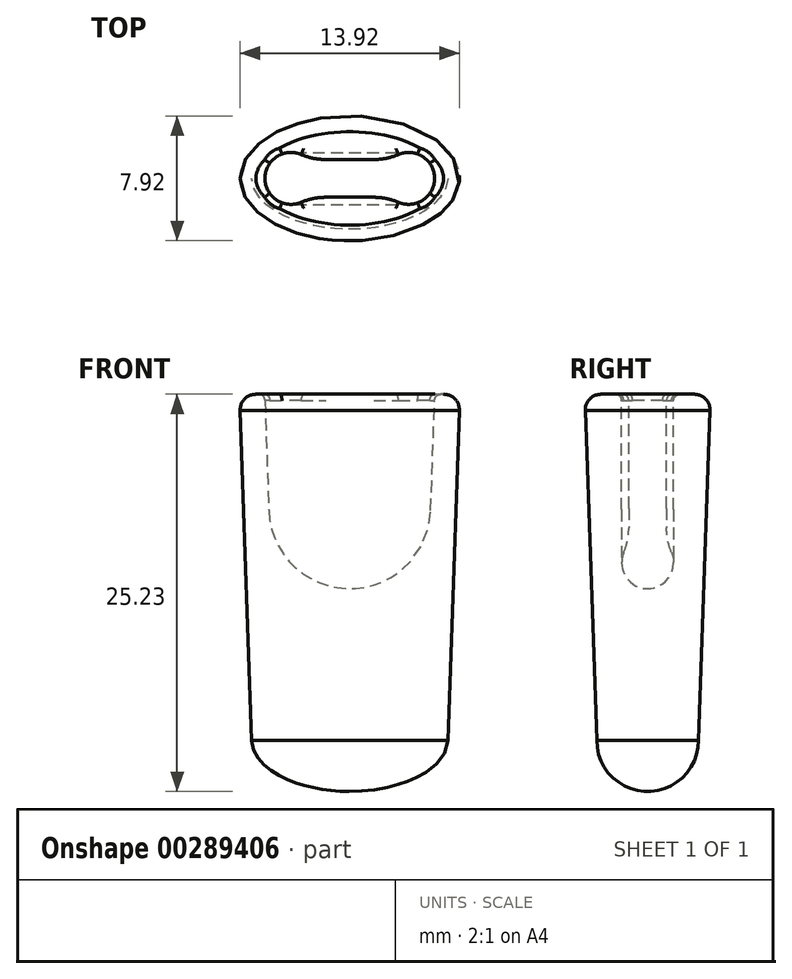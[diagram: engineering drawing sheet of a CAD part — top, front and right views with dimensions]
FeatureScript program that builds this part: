
annotation { "Feature Type Name" : "Feature", "Feature Type Description" : "" }
export const myFeature = defineFeature(function(context is Context, id is Id, definition is map)
    precondition{}
    {
        {
            var Q0;
            Q0=qCreatedBy(makeId("Front.planeOp"),FACE);
            var sketch = newSketch(context, id + "F0", { "sketchPlane" : qUnion([Q0])});
            skLineSegment(sketch, "E0", {"start": v(-3.78, 0.84) * mm, "end": v(-3.5, -7.33) * mm});
            skArc(sketch, "E1", {"start": v(-3.5, -7.33) * mm, "mid": v(-2.43, -9.72) * mm, "end": v(0, -10.7) * mm});
            skLineSegment(sketch, "E2", {"start": v(-3.78, 0.84) * mm, "end": v(-3.78, 1.56) * mm});
            skLineSegment(sketch, "E3", {"start": v(-3.75, 0) * mm, "end": v(0, 0) * mm, "construction": true});
            skLineSegment(sketch, "E4", {"start": v(-3.78, 1.56) * mm, "end": v(0, 1.56) * mm});
            skLineSegment(sketch, "E5.MirrorCS", {"start": v(3.78, 1.56) * mm, "end": v(0, 1.56) * mm});
            skLineSegment(sketch, "E6.MirrorCS", {"start": v(3.78, 0.84) * mm, "end": v(3.78, 1.56) * mm});
            skLineSegment(sketch, "E7.MirrorCS", {"start": v(3.75, 0) * mm, "end": v(0, 0) * mm, "construction": true});
            skLineSegment(sketch, "E8.MirrorCS", {"start": v(3.78, 0.84) * mm, "end": v(3.5, -7.33) * mm});
            skArc(sketch, "E9.MirrorCS", {"start": v(3.5, -7.33) * mm, "mid": v(2.43, -9.72) * mm, "end": v(0, -10.7) * mm});
            skSolve(sketch);
        }
        {
            var Q0;
            Q0=qCreatedBy(makeId("Top.planeOp"),FACE);
            var Q1;
            Q1=sQuery(id+"F0.wireOp",VERTEX,"E5.MirrorCS.end");
            cPlane(context, id + "F1", {"entities" : qUnion([Q0, Q1]), "cplaneType" : CPlaneType.PLANE_POINT, "offset" : 25 * mm, "width" : 150 * mm, "height" : 150 * mm});
        }
        {
            var Q0;
            Q0=qCreatedBy(id+"F1.planeOp",FACE);
            var sketch = newSketch(context, id + "F2", { "sketchPlane" : qUnion([Q0])});
            skCircle(sketch, "E10", {"center": v(-3.78, 0) * mm, "radius": 1.65 * mm});
            skSolve(sketch);
        }
        {
            var Q0;
            Q0=makeQuery(id+"F2.imprint","IMPRINT",FACE,{"disambiguationData":[TD([[makeQuery(id+"F2.imprint","IMPRINT",EDGE,{"derivedFrom":sQuery(id+"F2.wireOp",EDGE,"E10")}),1.0]])]});
            var Q1;
            Q1=sQuery(id+"F0.wireOp",EDGE,"E2");
            var Q2;
            Q2=sQuery(id+"F0.wireOp",EDGE,"E0");
            var Q3;
            Q3=sQuery(id+"F0.wireOp",EDGE,"E1");
            var Q4;
            Q4=sQuery(id+"F0.wireOp",EDGE,"E9.MirrorCS");
            var Q5;
            Q5=sQuery(id+"F0.wireOp",EDGE,"E8.MirrorCS");
            var Q6;
            Q6=sQuery(id+"F0.wireOp",EDGE,"E6.MirrorCS");
            sweep(context, id + "F3", {"profiles" : qUnion([Q0]), "path" : qUnion([Q1, Q2, Q3, Q4, Q5, Q6])});
        }
        {
            var Q0;
            Q0=makeQuery(id+"F0.imprint","IMPRINT",FACE,{"disambiguationData":[TD([[makeQuery(id+"F0.imprint","IMPRINT",EDGE,{"derivedFrom":sQuery(id+"F0.wireOp",EDGE,"E0")}),1.0]])]});
            extrude(context, id + "F4", {"entities" : qUnion([Q0]), "operationType" : NewBodyOperationType.ADD, "endBound" : BoundingType.SYMMETRIC, "depth" : 2.4 * mm});
        }
        {
            var Q0;
            {var subQ0=sQuery(id+"F0.wireOp",EDGE,"b3059032-d9f8-48f3-bb5a-612e4b6044fb0.MirrorCS");Q0=makeQuery(id+"F4.boolean.opBoolean","INTERSECT",EDGE,{"derivedFrom":[makeQuery(id+"F3.opSweep","SWEPT_FACE",FACE,{"disambiguationData":[OSD([subQ0,sQuery(id+"F2.wireOp",EDGE,"E10")])]}),makeQuery(id+"F4.opExtrude","CAP_FACE",FACE,{"disambiguationData":[OSD([sQuery(id+"F0.wireOp",EDGE,"E0"),sQuery(id+"F0.wireOp",EDGE,"E1"),subQ0,sQuery(id+"F0.wireOp",EDGE,"39ebad5e-6162-4d79-9b9c-69094e73386a0.MirrorCS"),sQuery(id+"F0.wireOp",EDGE,"sgdeaiES-GsHM-U3g8-oXAS-PtHumTGgpg0I")])],"isStart":true})]});}
            var Q1;
            {var subQ0=sQuery(id+"F0.wireOp",EDGE,"E0");Q1=makeQuery(id+"F4.boolean.opBoolean","INTERSECT",EDGE,{"derivedFrom":[makeQuery(id+"F3.opSweep","SWEPT_FACE",FACE,{"disambiguationData":[OSD([subQ0,sQuery(id+"F2.wireOp",EDGE,"E10")])]}),makeQuery(id+"F4.opExtrude","CAP_FACE",FACE,{"disambiguationData":[OSD([subQ0,sQuery(id+"F0.wireOp",EDGE,"E1"),sQuery(id+"F0.wireOp",EDGE,"b3059032-d9f8-48f3-bb5a-612e4b6044fb0.MirrorCS"),sQuery(id+"F0.wireOp",EDGE,"39ebad5e-6162-4d79-9b9c-69094e73386a0.MirrorCS"),sQuery(id+"F0.wireOp",EDGE,"sgdeaiES-GsHM-U3g8-oXAS-PtHumTGgpg0I")])],"isStart":true})]});}
            var Q2;
            {var subQ0=sQuery(id+"F0.wireOp",EDGE,"E1");Q2=makeQuery(id+"F4.boolean.opBoolean","INTERSECT",EDGE,{"derivedFrom":[makeQuery(id+"F3.opSweep","SWEPT_FACE",FACE,{"disambiguationData":[OSD([subQ0,sQuery(id+"F2.wireOp",EDGE,"E10")])]}),makeQuery(id+"F4.opExtrude","CAP_FACE",FACE,{"disambiguationData":[OSD([sQuery(id+"F0.wireOp",EDGE,"E0"),subQ0,sQuery(id+"F0.wireOp",EDGE,"b3059032-d9f8-48f3-bb5a-612e4b6044fb0.MirrorCS"),sQuery(id+"F0.wireOp",EDGE,"39ebad5e-6162-4d79-9b9c-69094e73386a0.MirrorCS"),sQuery(id+"F0.wireOp",EDGE,"sgdeaiES-GsHM-U3g8-oXAS-PtHumTGgpg0I")])],"isStart":true})]});}
            var Q3;
            {var subQ0=sQuery(id+"F0.wireOp",EDGE,"b3059032-d9f8-48f3-bb5a-612e4b6044fb0.MirrorCS");Q3=makeQuery(id+"F4.boolean.opBoolean","INTERSECT",EDGE,{"derivedFrom":[makeQuery(id+"F3.opSweep","SWEPT_FACE",FACE,{"disambiguationData":[OSD([subQ0,sQuery(id+"F2.wireOp",EDGE,"E10")])]}),makeQuery(id+"F4.opExtrude","CAP_FACE",FACE,{"disambiguationData":[OSD([sQuery(id+"F0.wireOp",EDGE,"E0"),sQuery(id+"F0.wireOp",EDGE,"E1"),subQ0,sQuery(id+"F0.wireOp",EDGE,"39ebad5e-6162-4d79-9b9c-69094e73386a0.MirrorCS"),sQuery(id+"F0.wireOp",EDGE,"sgdeaiES-GsHM-U3g8-oXAS-PtHumTGgpg0I")])],"isStart":false})]});}
            var Q4;
            {var subQ0=sQuery(id+"F0.wireOp",EDGE,"E0");Q4=makeQuery(id+"F4.boolean.opBoolean","INTERSECT",EDGE,{"derivedFrom":[makeQuery(id+"F3.opSweep","SWEPT_FACE",FACE,{"disambiguationData":[OSD([subQ0,sQuery(id+"F2.wireOp",EDGE,"E10")])]}),makeQuery(id+"F4.opExtrude","CAP_FACE",FACE,{"disambiguationData":[OSD([subQ0,sQuery(id+"F0.wireOp",EDGE,"E1"),sQuery(id+"F0.wireOp",EDGE,"b3059032-d9f8-48f3-bb5a-612e4b6044fb0.MirrorCS"),sQuery(id+"F0.wireOp",EDGE,"39ebad5e-6162-4d79-9b9c-69094e73386a0.MirrorCS"),sQuery(id+"F0.wireOp",EDGE,"sgdeaiES-GsHM-U3g8-oXAS-PtHumTGgpg0I")])],"isStart":false})]});}
            var Q5;
            {var subQ0=sQuery(id+"F0.wireOp",EDGE,"E1");Q5=makeQuery(id+"F4.boolean.opBoolean","INTERSECT",EDGE,{"derivedFrom":[makeQuery(id+"F3.opSweep","SWEPT_FACE",FACE,{"disambiguationData":[OSD([subQ0,sQuery(id+"F2.wireOp",EDGE,"E10")])]}),makeQuery(id+"F4.opExtrude","CAP_FACE",FACE,{"disambiguationData":[OSD([sQuery(id+"F0.wireOp",EDGE,"E0"),subQ0,sQuery(id+"F0.wireOp",EDGE,"b3059032-d9f8-48f3-bb5a-612e4b6044fb0.MirrorCS"),sQuery(id+"F0.wireOp",EDGE,"39ebad5e-6162-4d79-9b9c-69094e73386a0.MirrorCS"),sQuery(id+"F0.wireOp",EDGE,"sgdeaiES-GsHM-U3g8-oXAS-PtHumTGgpg0I")])],"isStart":false})]});}
            fillet(context, id + "F5", {"entities" : qUnion([Q0, Q1, Q2, Q3, Q4, Q5]), "radius" : 4 * mm, "tangentPropagation" : true, "allowEdgeOverflow" : false});
        }
        {
            var Q0;
            Q0=qCreatedBy(makeId("Top.planeOp"),FACE);
            var sketch = newSketch(context, id + "F6", { "sketchPlane" : qUnion([Q0])});
            skEllipse(sketch, "E11", {"center": v(0, 0) * mm, "majorRadius": 7 * mm, "minorRadius": 4 * mm, "majorAxis": v(1, 0)});
            skPoint(sketch, "E12", {"position": v(-7, 0) * mm});
            skSolve(sketch);
        }
        {
            var Q0;
            Q0=makeQuery(id+"F6.imprint","IMPRINT",FACE,{"disambiguationData":[TD([[makeQuery(id+"F6.imprint","IMPRINT",EDGE,{"derivedFrom":sQuery(id+"F6.wireOp",EDGE,"E11")}),1.0]])]});
            extrude(context, id + "F7", {"entities" : qUnion([Q0]), "oppositeDirection" : true, "depth" : 22 * mm, "hasDraft" : true, "draftAngle" : 2 * degree, "draftPullDirection" : true});
        }
        {
            var Q0;
            Q0=makeQuery(id+"F7.opExtrude","CAP_FACE",FACE,{"disambiguationData":[OSD([sQuery(id+"F6.wireOp",EDGE,"E11")])],"isStart":false});
            var sketch = newSketch(context, id + "F8", { "sketchPlane" : qUnion([Q0])});
            skLineSegment(sketch, "E13", {"start": v(-6.23, 0) * mm, "end": v(6.23, 0) * mm});
            skFitSpline(sketch, "E14", {"points": [v(-27.2, 0) * mm, v(-27.2, 0.3) * mm, v(-27.18, 0.62) * mm, v(-27.05, 1.24) * mm, v(-26.96, 1.56) * mm, v(-26.7, 2.22) * mm, v(-26.53, 2.56) * mm, v(-26.11, 3.25) * mm, v(-25.86, 3.6) * mm, v(-24.98, 4.67) * mm, v(-24.2, 5.4) * mm, v(-22.33, 6.8) * mm, v(-21.22, 7.48) * mm, v(-18.7, 8.74) * mm, v(-17.3, 9.31) * mm, v(-14.26, 10.33) * mm, v(-12.63, 10.77) * mm, v(-9.2, 11.48) * mm, v(-7.4, 11.75) * mm, v(-3.74, 12.11) * mm, v(-1.87, 12.2) * mm, v(1.87, 12.2) * mm, v(3.74, 12.11) * mm, v(7.4, 11.75) * mm, v(9.2, 11.48) * mm, v(12.63, 10.77) * mm, v(14.26, 10.33) * mm, v(17.3, 9.31) * mm, v(18.7, 8.74) * mm, v(21.22, 7.48) * mm, v(22.33, 6.8) * mm, v(24.2, 5.4) * mm, v(24.98, 4.67) * mm, v(25.86, 3.6) * mm, v(26.11, 3.25) * mm, v(26.53, 2.56) * mm, v(26.7, 2.22) * mm, v(26.96, 1.56) * mm, v(27.05, 1.24) * mm, v(27.18, 0.62) * mm, v(27.2, 0.3) * mm, v(27.2, 0) * mm, v(27.2, -0.3) * mm, v(27.18, -0.62) * mm, v(27.05, -1.24) * mm, v(26.96, -1.56) * mm, v(26.7, -2.22) * mm, v(26.53, -2.56) * mm, v(26.11, -3.25) * mm, v(25.86, -3.6) * mm, v(24.98, -4.67) * mm, v(24.2, -5.4) * mm, v(22.33, -6.8) * mm, v(21.22, -7.48) * mm, v(18.7, -8.74) * mm, v(17.3, -9.31) * mm, v(14.26, -10.33) * mm, v(12.63, -10.77) * mm, v(9.2, -11.48) * mm, v(7.4, -11.75) * mm, v(3.74, -12.11) * mm, v(1.87, -12.2) * mm, v(-1.87, -12.2) * mm, v(-3.74, -12.11) * mm, v(-7.4, -11.75) * mm, v(-9.2, -11.48) * mm, v(-12.63, -10.77) * mm, v(-14.26, -10.33) * mm, v(-17.3, -9.31) * mm, v(-18.7, -8.74) * mm, v(-21.22, -7.48) * mm, v(-22.33, -6.8) * mm, v(-24.2, -5.4) * mm, v(-24.98, -4.67) * mm, v(-25.86, -3.6) * mm, v(-26.11, -3.25) * mm, v(-26.53, -2.56) * mm, v(-26.7, -2.22) * mm, v(-26.96, -1.56) * mm, v(-27.05, -1.24) * mm, v(-27.18, -0.62) * mm, v(-27.2, -0.3) * mm, v(-27.2, 0) * mm]});
            skSolve(sketch);
        }
        {
            var Q0;
            Q0=makeQuery(id+"F8.imprint","IMPRINT",FACE,{"disambiguationData":[TD([[makeQuery(id+"F8.imprint","IMPRINT",EDGE,{"derivedFrom":sQuery(id+"F8.wireOp",EDGE,"E13")}),1.0]])]});
            var Q1;
            Q1=sQuery(id+"F8.wireOp",EDGE,"E13");
            revolve(context, id + "F9", {"operationType" : NewBodyOperationType.ADD, "entities" : qUnion([Q0]), "axis" : qUnion([Q1]), "revolveType" : RevolveType.ONE_DIRECTION, "angle" : 180 * degree});
        }
        {
            var Q0;
            Q0=makeQuery(id+"F3.opSweep","SWEPT_BODY",BODY,{"disambiguationData":[OSD([sQuery(id+"F0.wireOp",EDGE,"b3059032-d9f8-48f3-bb5a-612e4b6044fb0.MirrorCS"),sQuery(id+"F2.wireOp",EDGE,"E10")])]});
            var Q1;
            Q1=makeQuery(id+"F7.opExtrude","SWEPT_BODY",BODY,{"disambiguationData":[OSD([sQuery(id+"F6.wireOp",EDGE,"E11")])]});
            booleanBodies(context, id + "F10", {"operationType" : BooleanOperationType.SUBTRACTION, "tools" : qUnion([Q0]), "targets" : qUnion([Q1])});
        }
        {
            var Q0;
            Q0=makeQuery(id+"F7.opExtrude","CAP_EDGE",EDGE,{"disambiguationData":[OSD([sQuery(id+"F6.wireOp",EDGE,"E11")])],"isStart":true});
            fillet(context, id + "F11", {"entities" : qUnion([Q0]), "radius" : 1 * mm, "tangentPropagation" : true, "allowEdgeOverflow" : false});
        }
        {
            var Q0;
            Q0=makeQuery(id+"F10.opBoolean","INTERSECT",EDGE,{"derivedFrom":[makeQuery(id+"F3.opSweep","SWEPT_FACE",FACE,{"disambiguationData":[OSD([sQuery(id+"F0.wireOp",EDGE,"E0"),sQuery(id+"F2.wireOp",EDGE,"E10")])]}),makeQuery(id+"F7.opExtrude","CAP_FACE",FACE,{"disambiguationData":[OSD([sQuery(id+"F6.wireOp",EDGE,"E11")])],"isStart":true})]});
            var Q1;
            {var subQ0=sQuery(id+"F0.wireOp",EDGE,"E9.MirrorCS");var subQ1=sQuery(id+"F0.wireOp",EDGE,"E8.MirrorCS");var subQ2=sQuery(id+"F0.wireOp",EDGE,"E6.MirrorCS");var subQ3=sQuery(id+"F0.wireOp",EDGE,"E5.MirrorCS");var subQ4=sQuery(id+"F0.wireOp",EDGE,"E4");var subQ5=sQuery(id+"F0.wireOp",EDGE,"E2");var subQ6=sQuery(id+"F0.wireOp",EDGE,"E1");var subQ7=sQuery(id+"F0.wireOp",EDGE,"E0");var subQ8=sQuery(id+"F2.wireOp",EDGE,"E10");Q1=makeQuery(id+"F10.opBoolean","INTERSECT",EDGE,{"derivedFrom":[makeQuery(id+"F5.opFillet","BLEND_FACE",FACE,{"disambiguationData":[OSD([subQ7,subQ6,subQ5,subQ4,subQ3,subQ2,subQ1,subQ0,subQ8]),TDD([makeQuery(id+"F4.boolean.opBoolean","INTERSECT",EDGE,{"derivedFrom":[makeQuery(id+"F3.opSweep","SWEPT_FACE",FACE,{"disambiguationData":[OSD([subQ7,subQ8])]}),makeQuery(id+"F4.opExtrude","CAP_FACE",FACE,{"disambiguationData":[OSD([subQ7,subQ6,subQ5,subQ4,subQ3,subQ2,subQ1,subQ0])],"isStart":true})]})])]}),makeQuery(id+"F7.opExtrude","CAP_FACE",FACE,{"disambiguationData":[OSD([sQuery(id+"F6.wireOp",EDGE,"E11")])],"isStart":true})]});}
            var Q2;
            Q2=makeQuery(id+"F10.opBoolean","INTERSECT",EDGE,{"derivedFrom":[makeQuery(id+"F4.opExtrude","CAP_FACE",FACE,{"disambiguationData":[OSD([sQuery(id+"F0.wireOp",EDGE,"E0"),sQuery(id+"F0.wireOp",EDGE,"E1"),sQuery(id+"F0.wireOp",EDGE,"E2"),sQuery(id+"F0.wireOp",EDGE,"E4"),sQuery(id+"F0.wireOp",EDGE,"E5.MirrorCS"),sQuery(id+"F0.wireOp",EDGE,"E6.MirrorCS"),sQuery(id+"F0.wireOp",EDGE,"E8.MirrorCS"),sQuery(id+"F0.wireOp",EDGE,"E9.MirrorCS")])],"isStart":true}),makeQuery(id+"F7.opExtrude","CAP_FACE",FACE,{"disambiguationData":[OSD([sQuery(id+"F6.wireOp",EDGE,"E11")])],"isStart":true})]});
            var Q3;
            {var subQ0=sQuery(id+"F0.wireOp",EDGE,"E9.MirrorCS");var subQ1=sQuery(id+"F0.wireOp",EDGE,"E8.MirrorCS");var subQ2=sQuery(id+"F0.wireOp",EDGE,"E6.MirrorCS");var subQ3=sQuery(id+"F0.wireOp",EDGE,"E5.MirrorCS");var subQ4=sQuery(id+"F0.wireOp",EDGE,"E4");var subQ5=sQuery(id+"F0.wireOp",EDGE,"E2");var subQ6=sQuery(id+"F0.wireOp",EDGE,"E1");var subQ7=sQuery(id+"F0.wireOp",EDGE,"E0");var subQ8=sQuery(id+"F2.wireOp",EDGE,"E10");Q3=makeQuery(id+"F10.opBoolean","INTERSECT",EDGE,{"derivedFrom":[makeQuery(id+"F5.opFillet","BLEND_FACE",FACE,{"disambiguationData":[OSD([subQ7,subQ6,subQ5,subQ4,subQ3,subQ2,subQ1,subQ0,subQ8]),TDD([makeQuery(id+"F4.boolean.opBoolean","INTERSECT",EDGE,{"derivedFrom":[makeQuery(id+"F3.opSweep","SWEPT_FACE",FACE,{"disambiguationData":[OSD([subQ1,subQ8])]}),makeQuery(id+"F4.opExtrude","CAP_FACE",FACE,{"disambiguationData":[OSD([subQ7,subQ6,subQ5,subQ4,subQ3,subQ2,subQ1,subQ0])],"isStart":true})]})])]}),makeQuery(id+"F7.opExtrude","CAP_FACE",FACE,{"disambiguationData":[OSD([sQuery(id+"F6.wireOp",EDGE,"E11")])],"isStart":true})]});}
            var Q4;
            Q4=makeQuery(id+"F10.opBoolean","INTERSECT",EDGE,{"derivedFrom":[makeQuery(id+"F3.opSweep","SWEPT_FACE",FACE,{"disambiguationData":[OSD([sQuery(id+"F0.wireOp",EDGE,"E8.MirrorCS"),sQuery(id+"F2.wireOp",EDGE,"E10")])]}),makeQuery(id+"F7.opExtrude","CAP_FACE",FACE,{"disambiguationData":[OSD([sQuery(id+"F6.wireOp",EDGE,"E11")])],"isStart":true})]});
            var Q5;
            {var subQ0=sQuery(id+"F0.wireOp",EDGE,"E9.MirrorCS");var subQ1=sQuery(id+"F0.wireOp",EDGE,"E8.MirrorCS");var subQ2=sQuery(id+"F0.wireOp",EDGE,"E6.MirrorCS");var subQ3=sQuery(id+"F0.wireOp",EDGE,"E5.MirrorCS");var subQ4=sQuery(id+"F0.wireOp",EDGE,"E4");var subQ5=sQuery(id+"F0.wireOp",EDGE,"E2");var subQ6=sQuery(id+"F0.wireOp",EDGE,"E1");var subQ7=sQuery(id+"F0.wireOp",EDGE,"E0");var subQ8=sQuery(id+"F2.wireOp",EDGE,"E10");Q5=makeQuery(id+"F10.opBoolean","INTERSECT",EDGE,{"derivedFrom":[makeQuery(id+"F5.opFillet","BLEND_FACE",FACE,{"disambiguationData":[OSD([subQ7,subQ6,subQ5,subQ4,subQ3,subQ2,subQ1,subQ0,subQ8]),TDD([makeQuery(id+"F4.boolean.opBoolean","INTERSECT",EDGE,{"derivedFrom":[makeQuery(id+"F3.opSweep","SWEPT_FACE",FACE,{"disambiguationData":[OSD([subQ1,subQ8])]}),makeQuery(id+"F4.opExtrude","CAP_FACE",FACE,{"disambiguationData":[OSD([subQ7,subQ6,subQ5,subQ4,subQ3,subQ2,subQ1,subQ0])],"isStart":false})]})])]}),makeQuery(id+"F7.opExtrude","CAP_FACE",FACE,{"disambiguationData":[OSD([sQuery(id+"F6.wireOp",EDGE,"E11")])],"isStart":true})]});}
            var Q6;
            {var subQ0=sQuery(id+"F0.wireOp",EDGE,"E9.MirrorCS");var subQ1=sQuery(id+"F0.wireOp",EDGE,"E8.MirrorCS");var subQ2=sQuery(id+"F0.wireOp",EDGE,"E6.MirrorCS");var subQ3=sQuery(id+"F0.wireOp",EDGE,"E5.MirrorCS");var subQ4=sQuery(id+"F0.wireOp",EDGE,"E4");var subQ5=sQuery(id+"F0.wireOp",EDGE,"E2");var subQ6=sQuery(id+"F0.wireOp",EDGE,"E1");var subQ7=sQuery(id+"F0.wireOp",EDGE,"E0");var subQ8=sQuery(id+"F2.wireOp",EDGE,"E10");Q6=makeQuery(id+"F10.opBoolean","INTERSECT",EDGE,{"derivedFrom":[makeQuery(id+"F5.opFillet","BLEND_FACE",FACE,{"disambiguationData":[OSD([subQ7,subQ6,subQ5,subQ4,subQ3,subQ2,subQ1,subQ0,subQ8]),TDD([makeQuery(id+"F4.boolean.opBoolean","INTERSECT",EDGE,{"derivedFrom":[makeQuery(id+"F3.opSweep","SWEPT_FACE",FACE,{"disambiguationData":[OSD([subQ7,subQ8])]}),makeQuery(id+"F4.opExtrude","CAP_FACE",FACE,{"disambiguationData":[OSD([subQ7,subQ6,subQ5,subQ4,subQ3,subQ2,subQ1,subQ0])],"isStart":false})]})])]}),makeQuery(id+"F7.opExtrude","CAP_FACE",FACE,{"disambiguationData":[OSD([sQuery(id+"F6.wireOp",EDGE,"E11")])],"isStart":true})]});}
            fillet(context, id + "F12", {"entities" : qUnion([Q0, Q1, Q2, Q3, Q4, Q5, Q6]), "radius" : 0.4 * mm, "tangentPropagation" : true, "allowEdgeOverflow" : false});
        }
    });
